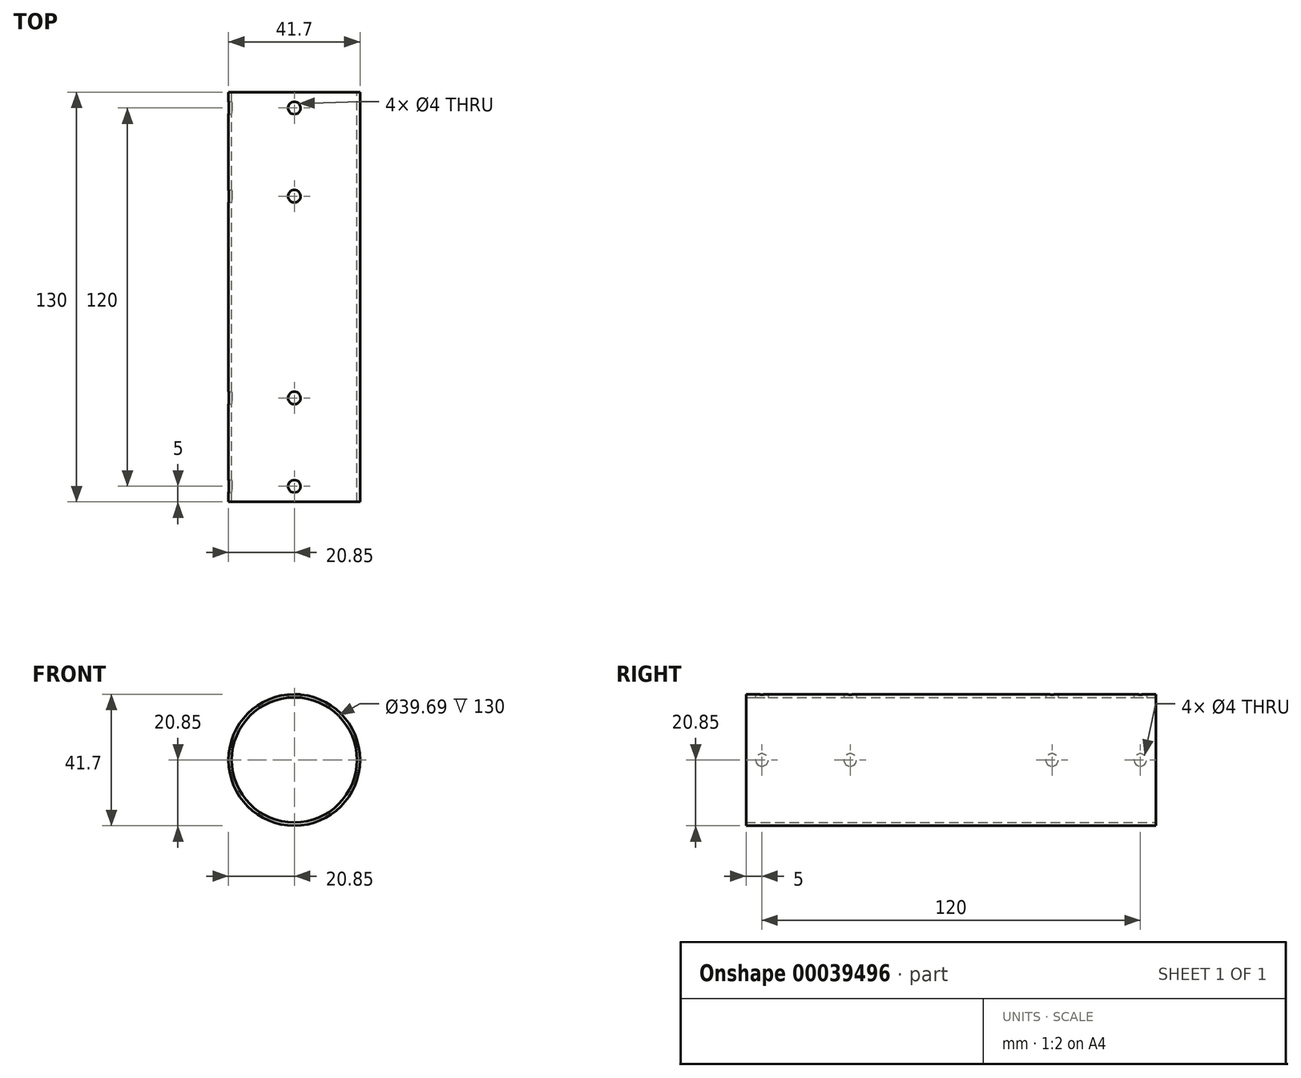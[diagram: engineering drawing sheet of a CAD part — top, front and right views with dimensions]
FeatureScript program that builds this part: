
annotation { "Feature Type Name" : "Feature", "Feature Type Description" : "" }
export const myFeature = defineFeature(function(context is Context, id is Id, definition is map)
    precondition{}
    {
        {
            assignVariable(context, id + "F0", {"name" : "length_body", "anyValue" : 50});
        }
        {
            assignVariable(context, id + "F1", {"name" : "length_conn", "anyValue" : 40});
        }
        {
            var Q0;
            Q0=qCreatedBy(makeId("Front.planeOp"),FACE);
            var sketch = newSketch(context, id + "F2", { "sketchPlane" : qUnion([Q0])});
            skCircle(sketch, "E0", {"center": v(0, 0) * mm, "radius": 19.85 * mm});
            skCircle(sketch, "E1.0", {"center": v(0, 0) * mm, "radius": 20.85 * mm});
            skSolve(sketch);
        }
        {
            var Q0;
            Q0=qSketchRegion(id+"F2",true);
            extrude(context, id + "F3", {"entities" : qUnion([Q0]), "endBound" : BoundingType.SYMMETRIC, "depth" : (getVariable(context, 'length_body')) * mm});
        }
        {
            var Q0;
            Q0=makeQuery(id+"F3.opExtrude","CAP_FACE",FACE,{"disambiguationData":[OSD([sQuery(id+"F2.wireOp",EDGE,"E0"),sQuery(id+"F2.wireOp",EDGE,"E1.0")])],"isStart":false});
            var sketch = newSketch(context, id + "F4", { "sketchPlane" : qUnion([Q0])});
            skCircle(sketch, "E2", {"center": v(0, 0) * mm, "radius": 19.85 * mm});
            skPoint(sketch, "E2.first.point", {"position": v(12.7, 15.26) * mm});
            skPoint(sketch, "E2.second.point", {"position": v(-15.87, -11.92) * mm});
            skPoint(sketch, "E2.third.point", {"position": v(9.03, -17.67) * mm});
            skCircle(sketch, "E3.0", {"center": v(0, 0) * mm, "radius": 20.85 * mm});
            skSolve(sketch);
        }
        {
            var Q0;
            Q0=qSketchRegion(id+"F4",true);
            extrude(context, id + "F5", {"entities" : qUnion([Q0]), "operationType" : NewBodyOperationType.ADD, "depth" : (getVariable(context, 'length_conn')) * mm});
        }
        {
            var Q0;
            Q0=qCreatedBy(makeId("Top.planeOp"),FACE);
            var sketch = newSketch(context, id + "F6", { "sketchPlane" : qUnion([Q0])});
            skCircle(sketch, "E4", {"center": v(0, -32) * mm, "radius": 2 * mm});
            skCircle(sketch, "E5", {"center": v(0, -60) * mm, "radius": 2 * mm});
            skSolve(sketch);
        }
        {
            var Q0;
            Q0=qCreatedBy(makeId("Right.planeOp"),FACE);
            var sketch = newSketch(context, id + "F7", { "sketchPlane" : qUnion([Q0])});
            skCircle(sketch, "E6", {"center": v(-60, 0) * mm, "radius": 2 * mm});
            skCircle(sketch, "E7", {"center": v(-32, 0) * mm, "radius": 2 * mm});
            skSolve(sketch);
        }
        {
            var Q0;
            Q0=makeQuery(id+"F3.opExtrude","CAP_FACE",FACE,{"disambiguationData":[OSD([sQuery(id+"F2.wireOp",EDGE,"E0"),sQuery(id+"F2.wireOp",EDGE,"E1.0")])],"isStart":true});
            var sketch = newSketch(context, id + "F8", { "sketchPlane" : qUnion([Q0])});
            skCircle(sketch, "E8", {"center": v(0, 0) * mm, "radius": 19.85 * mm});
            skPoint(sketch, "E8.first.point", {"position": v(7.6, 18.33) * mm});
            skPoint(sketch, "E8.second.point", {"position": v(19.85, 0) * mm});
            skPoint(sketch, "E8.third.point", {"position": v(9.7, -17.31) * mm});
            skCircle(sketch, "E9.0", {"center": v(0, 0) * mm, "radius": 20.85 * mm});
            skSolve(sketch);
        }
        {
            var Q0;
            Q0=qSketchRegion(id+"F8",true);
            extrude(context, id + "F9", {"entities" : qUnion([Q0]), "operationType" : NewBodyOperationType.ADD, "depth" : (getVariable(context, 'length_conn')) * mm});
        }
        {
            var Q0;
            Q0=qSketchRegion(id+"F6",true);
            extrude(context, id + "F10", {"entities" : qUnion([Q0]), "operationType" : NewBodyOperationType.REMOVE, "endBound" : BoundingType.THROUGH_ALL, "depth" : 19.63 * mm});
        }
        {
            var Q0;
            Q0=qSketchRegion(id+"F7",true);
            extrude(context, id + "F11", {"entities" : qUnion([Q0]), "operationType" : NewBodyOperationType.REMOVE, "endBound" : BoundingType.THROUGH_ALL, "oppositeDirection" : true, "depth" : 42.12 * mm});
        }
        {
            var Q0;
            Q0=qCreatedBy(makeId("Top.planeOp"),FACE);
            var sketch = newSketch(context, id + "F12", { "sketchPlane" : qUnion([Q0])});
            skCircle(sketch, "E10", {"center": v(0, 60) * mm, "radius": 2 * mm});
            skCircle(sketch, "E11", {"center": v(0, 32) * mm, "radius": 2 * mm});
            skSolve(sketch);
        }
        {
            var Q0;
            Q0=qSketchRegion(id+"F12",true);
            extrude(context, id + "F13", {"entities" : qUnion([Q0]), "operationType" : NewBodyOperationType.REMOVE, "endBound" : BoundingType.THROUGH_ALL, "depth" : 37.7 * mm});
        }
        {
            var Q0;
            Q0=qCreatedBy(makeId("Right.planeOp"),FACE);
            var sketch = newSketch(context, id + "F14", { "sketchPlane" : qUnion([Q0])});
            skCircle(sketch, "E12", {"center": v(60, 0) * mm, "radius": 2 * mm});
            skCircle(sketch, "E13", {"center": v(32, 0) * mm, "radius": 2 * mm});
            skSolve(sketch);
        }
        {
            var Q0;
            Q0=qSketchRegion(id+"F14",true);
            extrude(context, id + "F15", {"entities" : qUnion([Q0]), "operationType" : NewBodyOperationType.REMOVE, "endBound" : BoundingType.THROUGH_ALL, "oppositeDirection" : true, "depth" : 25 * mm});
        }
    });
